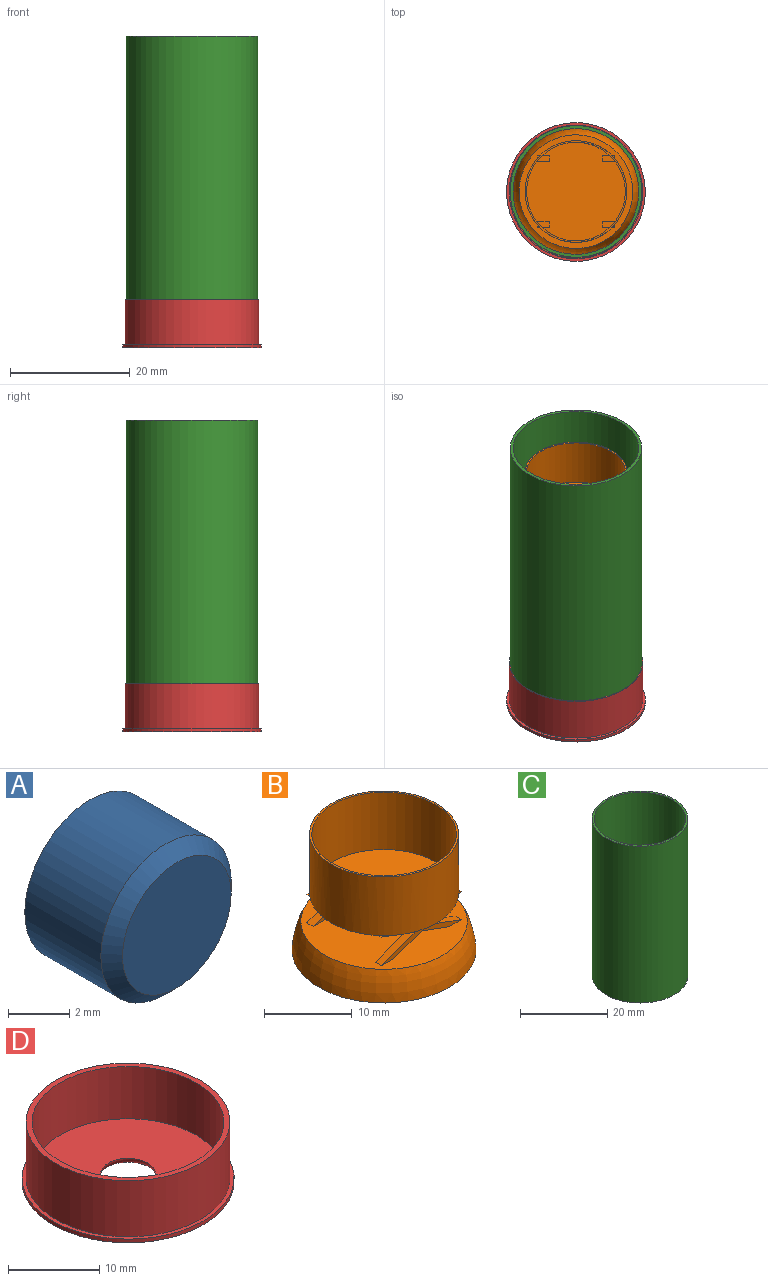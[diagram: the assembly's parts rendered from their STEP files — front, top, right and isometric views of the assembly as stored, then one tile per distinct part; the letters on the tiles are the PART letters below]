
ASSEMBLY  parts=4 mates=3
PART A: 4 faces, bbox 6x4x6 mm
  f0: cylinder r=3mm len=6mm, axis (0,1,0), area 66mm2, adj f2,f3
  f1: plane 5x5mm, normal (0,-1,0), area 19.6mm2, adj f2
  f2: cone r=2.5mm half-angle=45deg, axis (0,1,0), area 12.2mm2, adj f0,f1
  f3: plane 6x6mm, normal (0,1,0), area 28.3mm2, adj f0
PART B: 40 faces, bbox 21x21x16.2 mm
  f0: plane 17.01x17.01mm, normal (0,0,-1), area 219.3mm2, adj f1,f6,f7,f8,f9,f10,f11,f12
  f1: cylinder r=8.5mm len=17mm, axis (0,0,1), area 437.9mm2, adj f0,f2,f3,f4,f5,f37
  f2: plane 0.45x0.43mm, normal (0,0,1), area 0.1mm2, adj f1,f8,f21
  f3: plane 0.45x0.43mm, normal (0,0,1), area 0.1mm2, adj f1,f8,f18
  f4: plane 0.46x0.43mm, normal (0,0,1), area 0.1mm2, adj f1,f12,f25
  f5: plane 0.45x0.43mm, normal (0,0,1), area 0.1mm2, adj f1,f12,f26
  f6: plane 4.43x1.63mm, normal (0.34,0,0.94), area 4.7mm2, adj f0,f7,f8,f9
  f7: plane 4.43x1.63mm, normal (-0.34,0,0.94), area 4.7mm2, adj f0,f6,f8,f9
  f8: plane 12.89x4mm, normal (0,1,0), area 15.2mm2, adj f0,f2,f3,f6,f7,f14,f17,f18
  f9: plane 12.9x4mm, normal (0,-1,0), area 14.8mm2, adj f0,f6,f7,f14,f17,f18,f19,f20
  f10: plane 4.43x1.63mm, normal (-0.34,0,0.94), area 4.7mm2, adj f0,f11,f12,f13
  f11: plane 4.43x1.63mm, normal (0.34,0,0.94), area 4.7mm2, adj f0,f10,f12,f13
  f12: plane 12.89x4mm, normal (0,-1,0), area 15.2mm2, adj f0,f4,f5,f10,f11,f14,f25,f26
  f13: plane 12.89x4mm, normal (0,1,0), area 14.8mm2, adj f0,f10,f11,f14,f25,f26,f27,f28
  f14: plane 19x18.95mm, normal (0,0,1), area 275.5mm2, adj f8,f9,f12,f13,f16,f17,f19,f20
  f15: plane 21x21mm, normal (0,0,-1), area 77.5mm2, adj f16,f23,f24,f35
  f16: torus R=0.21mm, axis (0,0,1), area 264.3mm2, adj f14,f15,f24
  f17: plane 5.45x2mm, normal (-0.34,0,0.94), area 5.8mm2, adj f8,f9,f14,f18
  f18: plane 5.46x2.01mm, normal (-0.34,0,-0.94), area 5.8mm2, adj f0,f3,f8,f9,f17
  f19: plane 4.45x1.63mm, normal (-0.34,0,-0.94), area 4.7mm2, adj f8,f9,f14,f20
  f20: plane 4.45x1.63mm, normal (0.34,0,-0.94), area 4.7mm2, adj f8,f9,f14,f19
  f21: plane 5.45x2mm, normal (0.34,0,-0.94), area 5.8mm2, adj f0,f2,f8,f9,f22
  f22: plane 5.45x2mm, normal (0.34,0,0.94), area 5.8mm2, adj f8,f9,f14,f21
  f23: plane 4x2mm, normal (1,0,0), area 8mm2, adj f14,f15,f24
  f24: cylinder r=9.5mm len=4mm, axis (0,0,1), area 8mm2, adj f15,f16,f23
  f25: plane 5.46x2.01mm, normal (0.34,0,-0.94), area 5.8mm2, adj f0,f4,f12,f13,f30
  f26: plane 5.45x2mm, normal (-0.34,0,-0.94), area 5.8mm2, adj f0,f5,f12,f13,f27
  f27: plane 5.45x2mm, normal (-0.34,0,0.94), area 5.8mm2, adj f12,f13,f14,f26
  f28: plane 4.45x1.63mm, normal (0.34,0,-0.94), area 4.7mm2, adj f12,f13,f14,f29
  f29: plane 4.45x1.63mm, normal (-0.34,0,-0.94), area 4.7mm2, adj f12,f13,f14,f28
  f30: plane 5.45x2mm, normal (0.34,0,0.94), area 5.8mm2, adj f12,f13,f14,f25
  f31: plane 10x1.01mm, normal (0,0,-1), area 10.1mm2, adj f9,f13,f32,f34
  f32: plane 10x0.45mm, normal (1,0,0), area 4.5mm2, adj f9,f13,f31,f33
  f33: plane 10x1.01mm, normal (0,0,1), area 10.1mm2, adj f9,f13,f32,f34
  f34: plane 10x0.45mm, normal (-1,0,0), area 4.5mm2, adj f9,f13,f31,f33
  f35: cylinder r=9.25mm len=18.5mm, axis (0,0,-1), area 116.2mm2, adj f15,f36
  f36: plane 18.5x18.5mm, normal (0,0,-1), area 268.8mm2, adj f35
  f37: plane 17x17mm, normal (0,0,1), area 13.2mm2, adj f1,f38
  f38: cylinder r=8.25mm len=16.5mm, axis (0,0,1), area 414.7mm2, adj f37,f39
  f39: plane 16.5x16.5mm, normal (0,0,1), area 213.8mm2, adj f38
PART C: 4 faces, bbox 22x22x44 mm
  f0: cylinder r=11mm len=44mm, axis (0,0,-1), area 3041.1mm2, adj f1,f2
  f1: plane 22x22mm, normal (0,0,1), area 33.8mm2, adj f0,f3
  f2: plane 22x22mm, normal (0,0,-1), area 33.8mm2, adj f0,f3
  f3: cylinder r=10.5mm len=44mm, axis (0,0,1), area 2902.8mm2, adj f1,f2
PART D: 8 faces, bbox 23.2x23.2x8 mm
  f0: plane 23.2x23.2mm, normal (0,0,-1), area 372.5mm2, adj f1,f6
  f1: cylinder r=11.6mm len=23.2mm, axis (0,0,1), area 36.4mm2, adj f0,f2
  f2: plane 23.2x23.2mm, normal (0,0,1), area 32.2mm2, adj f1,f3
  f3: cylinder r=11.15mm len=22.3mm, axis (0,0,1), area 525.4mm2, adj f2,f7
  f4: cylinder r=10.5mm len=21mm, axis (0,0,1), area 461.8mm2, adj f5,f7
  f5: plane 21x21mm, normal (0,0,1), area 318.1mm2, adj f4,f6
  f6: torus R=4mm, axis (0,0,1), area 33.2mm2, adj f0,f5
  f7: plane 22.3x22.3mm, normal (0,0,1), area 44.2mm2, adj f3,f4
PLACE A rot(axis=(-1,0,0),90deg) t=(-62.37,62.72,-17.47)mm
PLACE B t=(-62.37,62.72,14.24)mm
PLACE C t=(-62.37,62.72,-12.76)mm
PLACE D t=(-62.37,62.72,-1.45)mm
MATE fastened B.f35 <-> D.f4  axis (0,0,-1) through (-62.37,62.72,10.24)mm
MATE fastened C.f3 <-> D.f4  axis (0,0,-1) through (-62.37,62.72,-12.76)mm
MATE fastened A.f0 <-> D.f6  axis (0,0,-1) through (-62.37,62.72,-20.47)mm
